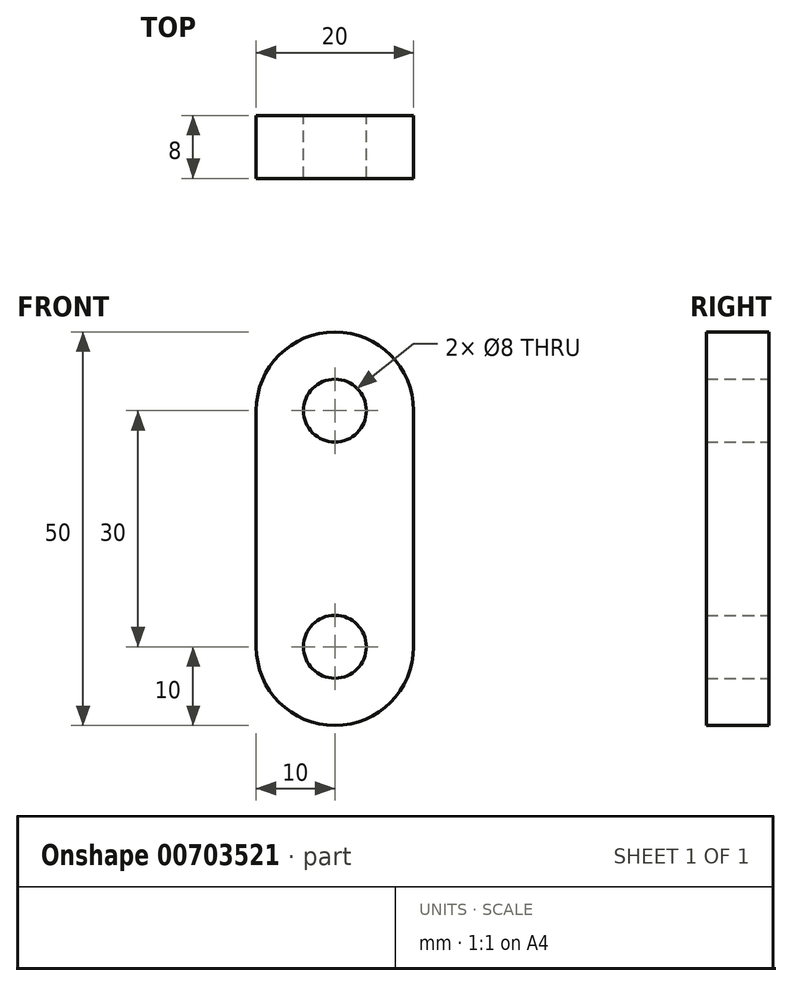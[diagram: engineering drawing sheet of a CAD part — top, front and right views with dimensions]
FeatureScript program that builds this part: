
annotation { "Feature Type Name" : "Feature", "Feature Type Description" : "" }
export const myFeature = defineFeature(function(context is Context, id is Id, definition is map)
    precondition{}
    {
        {
            var Q0;
            Q0=qCreatedBy(makeId("Front.planeOp"),FACE);
            var sketch = newSketch(context, id + "F0", { "sketchPlane" : qUnion([Q0])});
            skLineSegment(sketch, "E0.bottom", {"start": v(-10, 0) * mm, "end": v(10, 0) * mm});
            skLineSegment(sketch, "E0.left", {"start": v(-10, 0) * mm, "end": v(-10, 15) * mm});
            skLineSegment(sketch, "E0.right", {"start": v(10, 0) * mm, "end": v(10, 15) * mm});
            skArc(sketch, "E1", {"start": v(-10, 15) * mm, "mid": v(0, 25) * mm, "end": v(10, 15) * mm});
            skCircle(sketch, "E2", {"center": v(0, 15) * mm, "radius": 4 * mm});
            skLineSegment(sketch, "E3.MirrorCS", {"start": v(10, 0) * mm, "end": v(10, -15) * mm});
            skCircle(sketch, "E4.MirrorC", {"center": v(0, -15) * mm, "radius": 4 * mm});
            skArc(sketch, "E5.MirrorCS", {"start": v(-10, -15) * mm, "mid": v(0, -25) * mm, "end": v(10, -15) * mm});
            skLineSegment(sketch, "E6.MirrorCS", {"start": v(-10, 0) * mm, "end": v(-10, -15) * mm});
            skSolve(sketch);
        }
        {
            var Q0;
            Q0=makeQuery(id+"F0.imprint","IMPRINT",FACE,{"disambiguationData":[TD([[makeQuery(id+"F0.imprint","IMPRINT",EDGE,{"derivedFrom":sQuery(id+"F0.wireOp",EDGE,"E0.bottom")}),1.0]])]});
            var Q1;
            Q1=makeQuery(id+"F0.imprint","IMPRINT",FACE,{"disambiguationData":[TD([[makeQuery(id+"F0.imprint","IMPRINT",EDGE,{"derivedFrom":sQuery(id+"F0.wireOp",EDGE,"E0.bottom")}),-1.0]])]});
            extrude(context, id + "F1", {"entities" : qUnion([Q0, Q1]), "depth" : 8 * mm, "offsetDistance" : 25 * mm});
        }
    });
